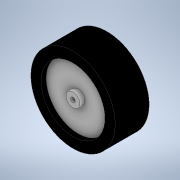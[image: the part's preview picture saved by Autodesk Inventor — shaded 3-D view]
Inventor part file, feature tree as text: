
AUTODESK INVENTOR PART (.ipt)
format: ipt  version: 2020 (Build 240168000, 168)  size: 139,776 bytes
history: native  units: mm
features: extrude x4, sketch x4, other x1, mirror x1
ambient origin geometry x8: Origin, YZ Plane, XZ Plane, XY Plane, X Axis, Y Axis, Z Axis, Center Point
bodies: Body1 (feature_tree)
feature tree (10):
  extrude  "Extrusão2"  Depth=26.6mm TaperAngle=0.0deg
  extrude  "Extrusão5"  Depth=4.0mm TaperAngle=0.0deg
  extrude  "Extrusão7"  Depth=4.0mm TaperAngle=0.0deg
  extrude  "Extrusão8"  TaperAngle=0.0deg  [1 undecoded]
  other  "Plano de trabalho1"
  mirror  "Espelhamento2"
  sketch  "Esboço2"  dims[d5=66.0mm d6=26.6mm d7=0.0mm]
  sketch  "Esboço9"  dims[d18=50.0mm d19=4.0mm d20=0.0mm]
  sketch  "Esboço12"  dims[d24=10.8mm d25=4.0mm d26=0.0mm]
  sketch  "Esboço13"  dims[d27=3.6mm d28=0.0mm d29=0.0mm d35=-13.3mm]
note: 1 required parameter value undecoded (feature->parameter linkage not recoverable at this tier; creation-order binding heuristic only, values carry confidence <= 0.55)
